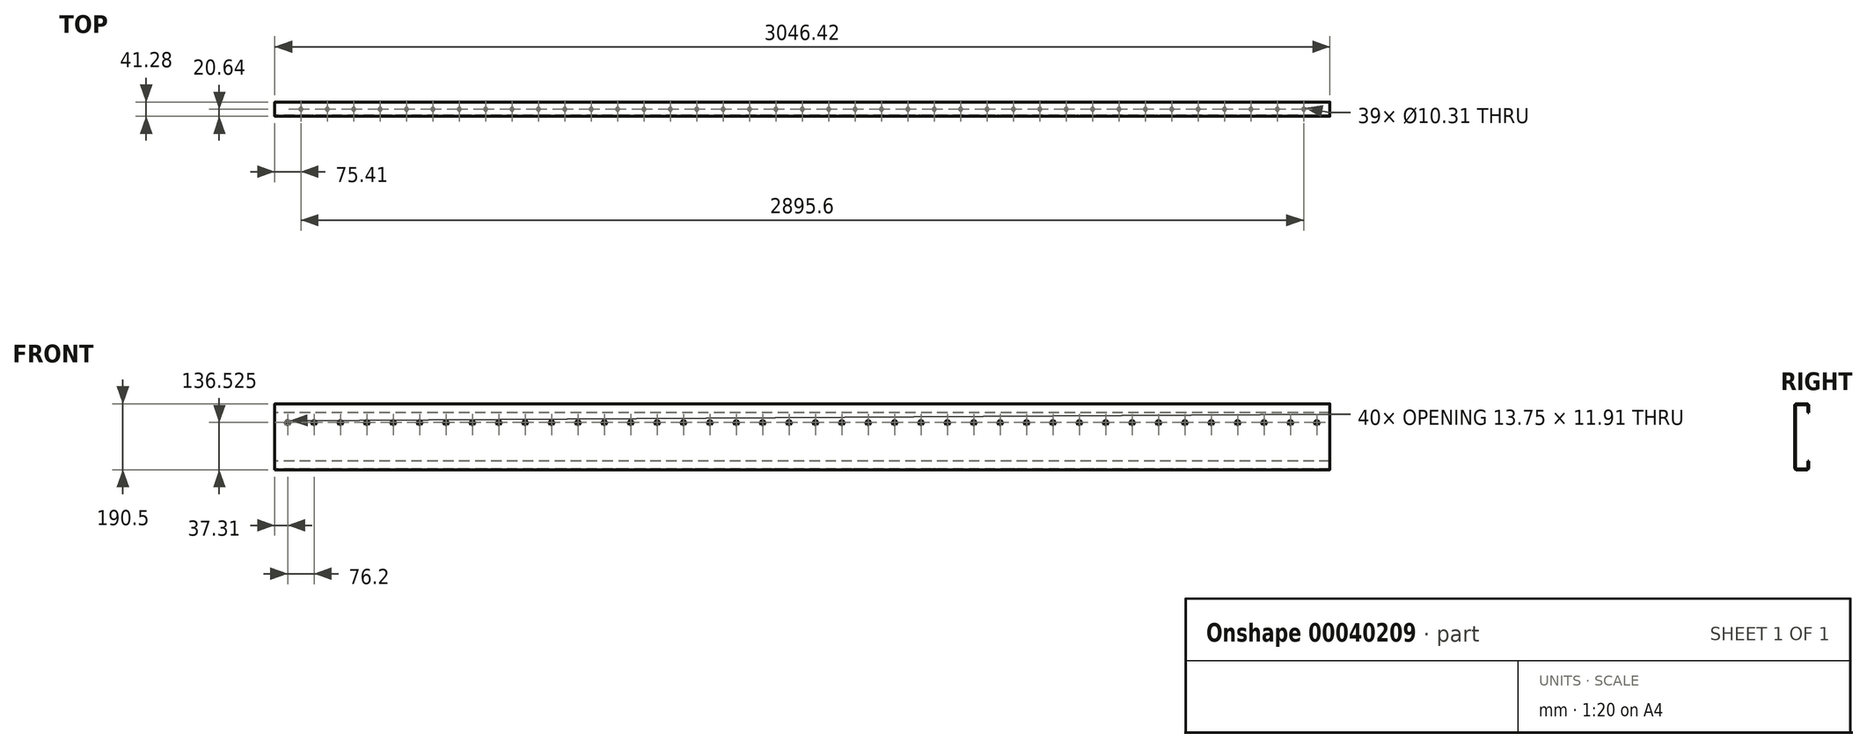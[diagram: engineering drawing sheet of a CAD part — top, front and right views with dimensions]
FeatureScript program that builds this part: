
annotation { "Feature Type Name" : "Feature", "Feature Type Description" : "" }
export const myFeature = defineFeature(function(context is Context, id is Id, definition is map)
    precondition{}
    {
        {
            var Q0;
            Q0=qCreatedBy(makeId("Right.planeOp"),FACE);
            var sketch = newSketch(context, id + "F0", { "sketchPlane" : qUnion([Q0])});
            skLineSegment(sketch, "E0", {"start": v(17.98, 69.85) * mm, "end": v(17.98, 89.42) * mm});
            skLineSegment(sketch, "E1", {"start": v(14.8, 92.6) * mm, "end": v(-14.8, 92.6) * mm});
            skLineSegment(sketch, "E2", {"start": v(-17.98, 89.42) * mm, "end": v(-17.98, -89.42) * mm});
            skLineSegment(sketch, "E3", {"start": v(-14.8, -92.6) * mm, "end": v(14.8, -92.6) * mm});
            skLineSegment(sketch, "E4", {"start": v(17.98, -89.42) * mm, "end": v(17.98, -69.85) * mm});
            skLineSegment(sketch, "E5.0", {"start": v(20.64, -88.9) * mm, "end": v(20.64, -69.85) * mm});
            skLineSegment(sketch, "E5.1", {"start": v(20.64, 69.85) * mm, "end": v(20.64, 88.9) * mm});
            skLineSegment(sketch, "E5.2", {"start": v(14.29, 95.25) * mm, "end": v(-14.29, 95.25) * mm});
            skLineSegment(sketch, "E5.3", {"start": v(-20.64, 88.9) * mm, "end": v(-20.64, -88.9) * mm});
            skLineSegment(sketch, "E5.4", {"start": v(-14.29, -95.25) * mm, "end": v(14.29, -95.25) * mm});
            skLineSegment(sketch, "E6", {"start": v(17.98, 69.85) * mm, "end": v(20.64, 69.85) * mm});
            skLineSegment(sketch, "E7", {"start": v(17.98, -69.85) * mm, "end": v(20.64, -69.85) * mm});
            skPoint(sketch, "E8.visualSharp", {"position": v(17.98, 92.6) * mm});
            skArc(sketch, "E8.filletArc", {"start": v(17.98, 89.42) * mm, "mid": v(17.05, 91.66) * mm, "end": v(14.8, 92.6) * mm});
            skPoint(sketch, "E9.visualSharp", {"position": v(17.98, -92.6) * mm});
            skArc(sketch, "E9.filletArc", {"start": v(14.8, -92.6) * mm, "mid": v(17.05, -91.66) * mm, "end": v(17.98, -89.42) * mm});
            skPoint(sketch, "E10.visualSharp", {"position": v(-17.98, -92.6) * mm});
            skArc(sketch, "E10.filletArc", {"start": v(-17.98, -89.42) * mm, "mid": v(-17.05, -91.66) * mm, "end": v(-14.8, -92.6) * mm});
            skPoint(sketch, "E11.visualSharp", {"position": v(-17.98, 92.6) * mm});
            skArc(sketch, "E11.filletArc", {"start": v(-14.8, 92.6) * mm, "mid": v(-17.05, 91.66) * mm, "end": v(-17.98, 89.42) * mm});
            skPoint(sketch, "E12.visualSharp", {"position": v(-20.64, 95.25) * mm});
            skArc(sketch, "E12.filletArc", {"start": v(-14.29, 95.25) * mm, "mid": v(-18.78, 93.4) * mm, "end": v(-20.64, 88.9) * mm});
            skPoint(sketch, "E13.visualSharp", {"position": v(20.64, 95.25) * mm});
            skArc(sketch, "E13.filletArc", {"start": v(20.64, 88.9) * mm, "mid": v(18.78, 93.4) * mm, "end": v(14.29, 95.25) * mm});
            skPoint(sketch, "E14.visualSharp", {"position": v(20.64, -95.25) * mm});
            skArc(sketch, "E14.filletArc", {"start": v(14.29, -95.25) * mm, "mid": v(18.78, -93.4) * mm, "end": v(20.64, -88.9) * mm});
            skPoint(sketch, "E15.visualSharp", {"position": v(-20.64, -95.25) * mm});
            skArc(sketch, "E15.filletArc", {"start": v(-20.64, -88.9) * mm, "mid": v(-18.78, -93.4) * mm, "end": v(-14.29, -95.25) * mm});
            skSolve(sketch);
        }
        {
            var Q0;
            Q0=makeQuery(id+"F0.imprint","IMPRINT",FACE,{"disambiguationData":[TD([[makeQuery(id+"F0.imprint","IMPRINT",EDGE,{"derivedFrom":sQuery(id+"F0.wireOp",EDGE,"E0")}),-1.0]])]});
            extrude(context, id + "F1", {"entities" : qUnion([Q0]), "endBound" : BoundingType.SYMMETRIC, "depth" : 3046.4 * mm});
        }
        {
            var Q0;
            Q0=makeQuery(id+"F1.opExtrude","SWEPT_FACE",FACE,{"disambiguationData":[OSD([sQuery(id+"F0.wireOp",EDGE,"E5.4")])]});
            var sketch = newSketch(context, id + "F2", { "sketchPlane" : qUnion([Q0])});
            skPoint(sketch, "E16", {"position": v(-1447.8, 0) * mm});
            skPoint(sketch, "E16.positionSnap0", {"position": v(-1523.2, 0) * mm});
            skPoint(sketch, "E17", {"position": v(-1371.6, 0) * mm});
            skPoint(sketch, "E18.1.0.0", {"position": v(-1295.4, 0) * mm});
            skPoint(sketch, "E18.2.0.0", {"position": v(-1219.2, 0) * mm});
            skPoint(sketch, "E18.3.0.0", {"position": v(-1143, 0) * mm});
            skPoint(sketch, "E18.4.0.0", {"position": v(-1066.8, 0) * mm});
            skPoint(sketch, "E18.5.0.0", {"position": v(-990.6, 0) * mm});
            skPoint(sketch, "E18.6.0.0", {"position": v(-914.4, 0) * mm});
            skPoint(sketch, "E18.7.0.0", {"position": v(-838.2, 0) * mm});
            skPoint(sketch, "E18.8.0.0", {"position": v(-762, 0) * mm});
            skPoint(sketch, "E18.9.0.0", {"position": v(-685.8, 0) * mm});
            skPoint(sketch, "E18.10.0.0", {"position": v(-609.6, 0) * mm});
            skPoint(sketch, "E18.11.0.0", {"position": v(-533.4, 0) * mm});
            skPoint(sketch, "E18.12.0.0", {"position": v(-457.2, 0) * mm});
            skPoint(sketch, "E18.13.0.0", {"position": v(-381, 0) * mm});
            skPoint(sketch, "E18.14.0.0", {"position": v(-304.8, 0) * mm});
            skPoint(sketch, "E18.15.0.0", {"position": v(-228.6, 0) * mm});
            skPoint(sketch, "E18.16.0.0", {"position": v(-152.4, 0) * mm});
            skPoint(sketch, "E18.17.0.0", {"position": v(-76.2, 0) * mm});
            skPoint(sketch, "E18.18.0.0", {"position": v(0, 0) * mm});
            skPoint(sketch, "E18.19.0.0", {"position": v(76.2, 0) * mm});
            skPoint(sketch, "E18.20.0.0", {"position": v(152.4, 0) * mm});
            skPoint(sketch, "E18.21.0.0", {"position": v(228.6, 0) * mm});
            skPoint(sketch, "E18.22.0.0", {"position": v(304.8, 0) * mm});
            skPoint(sketch, "E18.23.0.0", {"position": v(381, 0) * mm});
            skPoint(sketch, "E18.24.0.0", {"position": v(457.2, 0) * mm});
            skPoint(sketch, "E18.25.0.0", {"position": v(533.4, 0) * mm});
            skPoint(sketch, "E18.26.0.0", {"position": v(609.6, 0) * mm});
            skPoint(sketch, "E18.27.0.0", {"position": v(685.8, 0) * mm});
            skPoint(sketch, "E18.28.0.0", {"position": v(762, 0) * mm});
            skPoint(sketch, "E18.29.0.0", {"position": v(838.2, 0) * mm});
            skPoint(sketch, "E18.30.0.0", {"position": v(914.4, 0) * mm});
            skPoint(sketch, "E18.31.0.0", {"position": v(990.6, 0) * mm});
            skPoint(sketch, "E18.32.0.0", {"position": v(1066.8, 0) * mm});
            skPoint(sketch, "E18.33.0.0", {"position": v(1143, 0) * mm});
            skPoint(sketch, "E18.34.0.0", {"position": v(1219.2, 0) * mm});
            skLineSegment(sketch, "E18.direction1", {"start": v(-1371.6, 0) * mm, "end": v(-1295.4, 0) * mm, "construction": true});
            skPoint(sketch, "E19.0.35.0", {"position": v(1295.4, 0) * mm});
            skPoint(sketch, "E19.0.36.0", {"position": v(1371.6, 0) * mm});
            skPoint(sketch, "E20.0.37.0", {"position": v(1447.8, 0) * mm});
            skSolve(sketch);
        }
        {
            var Q0;
            Q0=sQuery(id+"F2.wireOp",VERTEX,"E16");
            var Q1;
            Q1=sQuery(id+"F2.wireOp",VERTEX,"E17");
            var Q2;
            Q2=sQuery(id+"F2.wireOp",VERTEX,"E18.1.0.0");
            var Q3;
            Q3=sQuery(id+"F2.wireOp",VERTEX,"E18.6.0.0");
            var Q4;
            Q4=sQuery(id+"F2.wireOp",VERTEX,"E18.7.0.0");
            var Q5;
            Q5=sQuery(id+"F2.wireOp",VERTEX,"E18.8.0.0");
            var Q6;
            Q6=sQuery(id+"F2.wireOp",VERTEX,"E18.9.0.0");
            var Q7;
            Q7=sQuery(id+"F2.wireOp",VERTEX,"E18.10.0.0");
            var Q8;
            Q8=sQuery(id+"F2.wireOp",VERTEX,"E18.11.0.0");
            var Q9;
            Q9=sQuery(id+"F2.wireOp",VERTEX,"E18.2.0.0");
            var Q10;
            Q10=sQuery(id+"F2.wireOp",VERTEX,"E18.5.0.0");
            var Q11;
            Q11=sQuery(id+"F2.wireOp",VERTEX,"E18.4.0.0");
            var Q12;
            Q12=sQuery(id+"F2.wireOp",VERTEX,"E18.3.0.0");
            var Q13;
            Q13=sQuery(id+"F2.wireOp",VERTEX,"E18.24.0.0");
            var Q14;
            Q14=sQuery(id+"F2.wireOp",VERTEX,"E18.23.0.0");
            var Q15;
            Q15=sQuery(id+"F2.wireOp",VERTEX,"E18.28.0.0");
            var Q16;
            Q16=sQuery(id+"F2.wireOp",VERTEX,"E18.22.0.0");
            var Q17;
            Q17=sQuery(id+"F2.wireOp",VERTEX,"E20.0.37.0");
            var Q18;
            Q18=sQuery(id+"F2.wireOp",VERTEX,"E18.21.0.0");
            var Q19;
            Q19=sQuery(id+"F2.wireOp",VERTEX,"E19.0.36.0");
            var Q20;
            Q20=sQuery(id+"F2.wireOp",VERTEX,"E18.20.0.0");
            var Q21;
            Q21=sQuery(id+"F2.wireOp",VERTEX,"E19.0.35.0");
            var Q22;
            Q22=sQuery(id+"F2.wireOp",VERTEX,"E18.19.0.0");
            var Q23;
            Q23=sQuery(id+"F2.wireOp",VERTEX,"E18.18.0.0");
            var Q24;
            Q24=sQuery(id+"F2.wireOp",VERTEX,"E18.17.0.0");
            var Q25;
            Q25=sQuery(id+"F2.wireOp",VERTEX,"E18.34.0.0");
            var Q26;
            Q26=sQuery(id+"F2.wireOp",VERTEX,"E18.27.0.0");
            var Q27;
            Q27=sQuery(id+"F2.wireOp",VERTEX,"E18.16.0.0");
            var Q28;
            Q28=sQuery(id+"F2.wireOp",VERTEX,"E18.33.0.0");
            var Q29;
            Q29=sQuery(id+"F2.wireOp",VERTEX,"E18.26.0.0");
            var Q30;
            Q30=sQuery(id+"F2.wireOp",VERTEX,"E18.15.0.0");
            var Q31;
            Q31=sQuery(id+"F2.wireOp",VERTEX,"E18.25.0.0");
            var Q32;
            Q32=sQuery(id+"F2.wireOp",VERTEX,"E18.32.0.0");
            var Q33;
            Q33=sQuery(id+"F2.wireOp",VERTEX,"E18.14.0.0");
            var Q34;
            Q34=sQuery(id+"F2.wireOp",VERTEX,"E18.31.0.0");
            var Q35;
            Q35=sQuery(id+"F2.wireOp",VERTEX,"E18.13.0.0");
            var Q36;
            Q36=sQuery(id+"F2.wireOp",VERTEX,"E18.30.0.0");
            var Q37;
            Q37=sQuery(id+"F2.wireOp",VERTEX,"E18.12.0.0");
            var Q38;
            Q38=sQuery(id+"F2.wireOp",VERTEX,"E18.29.0.0");
            var Q39;
            Q39=makeQuery(id+"F1.opExtrude","SWEPT_BODY",BODY,{"disambiguationData":[OSD([sQuery(id+"F0.wireOp",EDGE,"E0"),sQuery(id+"F0.wireOp",EDGE,"E1"),sQuery(id+"F0.wireOp",EDGE,"E2"),sQuery(id+"F0.wireOp",EDGE,"E3"),sQuery(id+"F0.wireOp",EDGE,"E4"),sQuery(id+"F0.wireOp",EDGE,"E5.0"),sQuery(id+"F0.wireOp",EDGE,"E5.1"),sQuery(id+"F0.wireOp",EDGE,"E5.2"),sQuery(id+"F0.wireOp",EDGE,"E5.3"),sQuery(id+"F0.wireOp",EDGE,"E5.4"),sQuery(id+"F0.wireOp",EDGE,"E6"),sQuery(id+"F0.wireOp",EDGE,"E7"),sQuery(id+"F0.wireOp",EDGE,"E8.filletArc"),sQuery(id+"F0.wireOp",EDGE,"E9.filletArc"),sQuery(id+"F0.wireOp",EDGE,"E10.filletArc"),sQuery(id+"F0.wireOp",EDGE,"E11.filletArc"),sQuery(id+"F0.wireOp",EDGE,"E12.filletArc"),sQuery(id+"F0.wireOp",EDGE,"E13.filletArc"),sQuery(id+"F0.wireOp",EDGE,"E14.filletArc"),sQuery(id+"F0.wireOp",EDGE,"E15.filletArc")])]});
            hole(context, id + "F3", {"style" : HoleStyle.SIMPLE, "holeDiameter" : 10.3 * mm, "endStyle" : HoleEndStyle.BLIND, "holeDepth" : 38.1 * mm, "locations" : qUnion([Q0, Q1, Q2, Q3, Q4, Q5, Q6, Q7, Q8, Q9, Q10, Q11, Q12, Q13, Q14, Q15, Q16, Q17, Q18, Q19, Q20, Q21, Q22, Q23, Q24, Q25, Q26, Q27, Q28, Q29, Q30, Q31, Q32, Q33, Q34, Q35, Q36, Q37, Q38]), "scope" : qUnion([Q39])});
        }
        {
            var Q0;
            Q0=makeQuery(id+"F1.opExtrude","SWEPT_FACE",FACE,{"disambiguationData":[OSD([sQuery(id+"F0.wireOp",EDGE,"E5.3")])]});
            var sketch = newSketch(context, id + "F4", { "sketchPlane" : qUnion([Q0])});
            skLineSegment(sketch, "E21", {"start": v(-1523.2, 41.28) * mm, "end": v(-1485.9, 41.28) * mm, "construction": true});
            skLineSegment(sketch, "E22.0", {"start": v(1523.2, 95.25) * mm, "end": v(-1523.2, 95.25) * mm, "construction": true});
            skCircle(sketch, "E23.cCircle", {"center": v(-1485.9, 41.28) * mm, "radius": 6.87 * mm, "construction": true});
            skLineSegment(sketch, "E23.0", {"start": v(-1492.77, 41.27) * mm, "end": v(-1489.34, 47.23) * mm});
            skLineSegment(sketch, "E23.1", {"start": v(-1489.34, 47.23) * mm, "end": v(-1482.46, 47.23) * mm});
            skLineSegment(sketch, "E23.2", {"start": v(-1482.46, 47.23) * mm, "end": v(-1479.03, 41.27) * mm});
            skLineSegment(sketch, "E23.3", {"start": v(-1479.03, 41.27) * mm, "end": v(-1482.46, 35.32) * mm});
            skLineSegment(sketch, "E23.4", {"start": v(-1482.46, 35.32) * mm, "end": v(-1489.34, 35.32) * mm});
            skLineSegment(sketch, "E23.5", {"start": v(-1489.34, 35.32) * mm, "end": v(-1492.77, 41.27) * mm});
            skLineSegment(sketch, "E24.1.0.0", {"start": v(-1406.26, 35.32) * mm, "end": v(-1413.14, 35.32) * mm});
            skLineSegment(sketch, "E24.1.0.1", {"start": v(-1402.83, 41.28) * mm, "end": v(-1406.26, 35.32) * mm});
            skLineSegment(sketch, "E24.1.0.2", {"start": v(-1413.14, 47.23) * mm, "end": v(-1406.26, 47.23) * mm});
            skLineSegment(sketch, "E24.1.0.3", {"start": v(-1406.26, 47.23) * mm, "end": v(-1402.83, 41.27) * mm});
            skCircle(sketch, "E24.1.0.4", {"center": v(-1409.7, 41.28) * mm, "radius": 6.87 * mm, "construction": true});
            skLineSegment(sketch, "E24.1.0.5", {"start": v(-1413.14, 35.32) * mm, "end": v(-1416.57, 41.27) * mm});
            skLineSegment(sketch, "E24.1.0.6", {"start": v(-1416.57, 41.28) * mm, "end": v(-1413.14, 47.23) * mm});
            skLineSegment(sketch, "E24.2.0.0", {"start": v(-1330.06, 35.32) * mm, "end": v(-1336.94, 35.32) * mm});
            skLineSegment(sketch, "E24.2.0.1", {"start": v(-1326.63, 41.28) * mm, "end": v(-1330.06, 35.32) * mm});
            skLineSegment(sketch, "E24.2.0.2", {"start": v(-1336.94, 47.23) * mm, "end": v(-1330.06, 47.23) * mm});
            skLineSegment(sketch, "E24.2.0.3", {"start": v(-1330.06, 47.23) * mm, "end": v(-1326.63, 41.27) * mm});
            skCircle(sketch, "E24.2.0.4", {"center": v(-1333.5, 41.28) * mm, "radius": 6.87 * mm, "construction": true});
            skLineSegment(sketch, "E24.2.0.5", {"start": v(-1336.94, 35.32) * mm, "end": v(-1340.37, 41.27) * mm});
            skLineSegment(sketch, "E24.2.0.6", {"start": v(-1340.37, 41.28) * mm, "end": v(-1336.94, 47.23) * mm});
            skLineSegment(sketch, "E24.3.0.0", {"start": v(-1253.86, 35.32) * mm, "end": v(-1260.74, 35.32) * mm});
            skLineSegment(sketch, "E24.3.0.1", {"start": v(-1250.43, 41.28) * mm, "end": v(-1253.86, 35.32) * mm});
            skLineSegment(sketch, "E24.3.0.2", {"start": v(-1260.74, 47.23) * mm, "end": v(-1253.86, 47.23) * mm});
            skLineSegment(sketch, "E24.3.0.3", {"start": v(-1253.86, 47.23) * mm, "end": v(-1250.43, 41.27) * mm});
            skCircle(sketch, "E24.3.0.4", {"center": v(-1257.3, 41.28) * mm, "radius": 6.87 * mm, "construction": true});
            skLineSegment(sketch, "E24.3.0.5", {"start": v(-1260.74, 35.32) * mm, "end": v(-1264.17, 41.27) * mm});
            skLineSegment(sketch, "E24.3.0.6", {"start": v(-1264.17, 41.28) * mm, "end": v(-1260.74, 47.23) * mm});
            skLineSegment(sketch, "E24.4.0.0", {"start": v(-1177.66, 35.32) * mm, "end": v(-1184.54, 35.32) * mm});
            skLineSegment(sketch, "E24.4.0.1", {"start": v(-1174.23, 41.28) * mm, "end": v(-1177.66, 35.32) * mm});
            skLineSegment(sketch, "E24.4.0.2", {"start": v(-1184.54, 47.23) * mm, "end": v(-1177.66, 47.23) * mm});
            skLineSegment(sketch, "E24.4.0.3", {"start": v(-1177.66, 47.23) * mm, "end": v(-1174.23, 41.27) * mm});
            skCircle(sketch, "E24.4.0.4", {"center": v(-1181.1, 41.28) * mm, "radius": 6.87 * mm, "construction": true});
            skLineSegment(sketch, "E24.4.0.5", {"start": v(-1184.54, 35.32) * mm, "end": v(-1187.97, 41.27) * mm});
            skLineSegment(sketch, "E24.4.0.6", {"start": v(-1187.97, 41.28) * mm, "end": v(-1184.54, 47.23) * mm});
            skLineSegment(sketch, "E24.5.0.0", {"start": v(-1101.46, 35.32) * mm, "end": v(-1108.34, 35.32) * mm});
            skLineSegment(sketch, "E24.5.0.1", {"start": v(-1098.03, 41.28) * mm, "end": v(-1101.46, 35.32) * mm});
            skLineSegment(sketch, "E24.5.0.2", {"start": v(-1108.34, 47.23) * mm, "end": v(-1101.46, 47.23) * mm});
            skLineSegment(sketch, "E24.5.0.3", {"start": v(-1101.46, 47.23) * mm, "end": v(-1098.03, 41.27) * mm});
            skCircle(sketch, "E24.5.0.4", {"center": v(-1104.9, 41.28) * mm, "radius": 6.87 * mm, "construction": true});
            skLineSegment(sketch, "E24.5.0.5", {"start": v(-1108.34, 35.32) * mm, "end": v(-1111.77, 41.27) * mm});
            skLineSegment(sketch, "E24.5.0.6", {"start": v(-1111.77, 41.28) * mm, "end": v(-1108.34, 47.23) * mm});
            skLineSegment(sketch, "E24.6.0.0", {"start": v(-1025.26, 35.32) * mm, "end": v(-1032.14, 35.32) * mm});
            skLineSegment(sketch, "E24.6.0.1", {"start": v(-1021.83, 41.28) * mm, "end": v(-1025.26, 35.32) * mm});
            skLineSegment(sketch, "E24.6.0.2", {"start": v(-1032.14, 47.23) * mm, "end": v(-1025.26, 47.23) * mm});
            skLineSegment(sketch, "E24.6.0.3", {"start": v(-1025.26, 47.23) * mm, "end": v(-1021.83, 41.27) * mm});
            skCircle(sketch, "E24.6.0.4", {"center": v(-1028.7, 41.28) * mm, "radius": 6.87 * mm, "construction": true});
            skLineSegment(sketch, "E24.6.0.5", {"start": v(-1032.14, 35.32) * mm, "end": v(-1035.57, 41.27) * mm});
            skLineSegment(sketch, "E24.6.0.6", {"start": v(-1035.57, 41.28) * mm, "end": v(-1032.14, 47.23) * mm});
            skLineSegment(sketch, "E24.7.0.0", {"start": v(-949.06, 35.32) * mm, "end": v(-955.94, 35.32) * mm});
            skLineSegment(sketch, "E24.7.0.1", {"start": v(-945.63, 41.28) * mm, "end": v(-949.06, 35.32) * mm});
            skLineSegment(sketch, "E24.7.0.2", {"start": v(-955.94, 47.23) * mm, "end": v(-949.06, 47.23) * mm});
            skLineSegment(sketch, "E24.7.0.3", {"start": v(-949.06, 47.23) * mm, "end": v(-945.63, 41.27) * mm});
            skCircle(sketch, "E24.7.0.4", {"center": v(-952.5, 41.28) * mm, "radius": 6.87 * mm, "construction": true});
            skLineSegment(sketch, "E24.7.0.5", {"start": v(-955.94, 35.32) * mm, "end": v(-959.37, 41.27) * mm});
            skLineSegment(sketch, "E24.7.0.6", {"start": v(-959.37, 41.28) * mm, "end": v(-955.94, 47.23) * mm});
            skLineSegment(sketch, "E24.8.0.0", {"start": v(-872.86, 35.32) * mm, "end": v(-879.74, 35.32) * mm});
            skLineSegment(sketch, "E24.8.0.1", {"start": v(-869.43, 41.28) * mm, "end": v(-872.86, 35.32) * mm});
            skLineSegment(sketch, "E24.8.0.2", {"start": v(-879.74, 47.23) * mm, "end": v(-872.86, 47.23) * mm});
            skLineSegment(sketch, "E24.8.0.3", {"start": v(-872.86, 47.23) * mm, "end": v(-869.43, 41.27) * mm});
            skCircle(sketch, "E24.8.0.4", {"center": v(-876.3, 41.28) * mm, "radius": 6.87 * mm, "construction": true});
            skLineSegment(sketch, "E24.8.0.5", {"start": v(-879.74, 35.32) * mm, "end": v(-883.17, 41.27) * mm});
            skLineSegment(sketch, "E24.8.0.6", {"start": v(-883.17, 41.28) * mm, "end": v(-879.74, 47.23) * mm});
            skLineSegment(sketch, "E24.9.0.0", {"start": v(-796.66, 35.32) * mm, "end": v(-803.54, 35.32) * mm});
            skLineSegment(sketch, "E24.9.0.1", {"start": v(-793.23, 41.28) * mm, "end": v(-796.66, 35.32) * mm});
            skLineSegment(sketch, "E24.9.0.2", {"start": v(-803.54, 47.23) * mm, "end": v(-796.66, 47.23) * mm});
            skLineSegment(sketch, "E24.9.0.3", {"start": v(-796.66, 47.23) * mm, "end": v(-793.23, 41.27) * mm});
            skCircle(sketch, "E24.9.0.4", {"center": v(-800.1, 41.28) * mm, "radius": 6.87 * mm, "construction": true});
            skLineSegment(sketch, "E24.9.0.5", {"start": v(-803.54, 35.32) * mm, "end": v(-806.97, 41.27) * mm});
            skLineSegment(sketch, "E24.9.0.6", {"start": v(-806.97, 41.28) * mm, "end": v(-803.54, 47.23) * mm});
            skLineSegment(sketch, "E24.10.0.0", {"start": v(-720.46, 35.32) * mm, "end": v(-727.34, 35.32) * mm});
            skLineSegment(sketch, "E24.10.0.1", {"start": v(-717.03, 41.28) * mm, "end": v(-720.46, 35.32) * mm});
            skLineSegment(sketch, "E24.10.0.2", {"start": v(-727.34, 47.23) * mm, "end": v(-720.46, 47.23) * mm});
            skLineSegment(sketch, "E24.10.0.3", {"start": v(-720.46, 47.23) * mm, "end": v(-717.03, 41.27) * mm});
            skCircle(sketch, "E24.10.0.4", {"center": v(-723.9, 41.28) * mm, "radius": 6.87 * mm, "construction": true});
            skLineSegment(sketch, "E24.10.0.5", {"start": v(-727.34, 35.32) * mm, "end": v(-730.77, 41.27) * mm});
            skLineSegment(sketch, "E24.10.0.6", {"start": v(-730.77, 41.28) * mm, "end": v(-727.34, 47.23) * mm});
            skLineSegment(sketch, "E24.11.0.0", {"start": v(-644.26, 35.32) * mm, "end": v(-651.14, 35.32) * mm});
            skLineSegment(sketch, "E24.11.0.1", {"start": v(-640.83, 41.28) * mm, "end": v(-644.26, 35.32) * mm});
            skLineSegment(sketch, "E24.11.0.2", {"start": v(-651.14, 47.23) * mm, "end": v(-644.26, 47.23) * mm});
            skLineSegment(sketch, "E24.11.0.3", {"start": v(-644.26, 47.23) * mm, "end": v(-640.83, 41.27) * mm});
            skCircle(sketch, "E24.11.0.4", {"center": v(-647.7, 41.28) * mm, "radius": 6.87 * mm, "construction": true});
            skLineSegment(sketch, "E24.11.0.5", {"start": v(-651.14, 35.32) * mm, "end": v(-654.57, 41.27) * mm});
            skLineSegment(sketch, "E24.11.0.6", {"start": v(-654.57, 41.28) * mm, "end": v(-651.14, 47.23) * mm});
            skLineSegment(sketch, "E24.12.0.0", {"start": v(-568.06, 35.32) * mm, "end": v(-574.94, 35.32) * mm});
            skLineSegment(sketch, "E24.12.0.1", {"start": v(-564.63, 41.28) * mm, "end": v(-568.06, 35.32) * mm});
            skLineSegment(sketch, "E24.12.0.2", {"start": v(-574.94, 47.23) * mm, "end": v(-568.06, 47.23) * mm});
            skLineSegment(sketch, "E24.12.0.3", {"start": v(-568.06, 47.23) * mm, "end": v(-564.63, 41.27) * mm});
            skCircle(sketch, "E24.12.0.4", {"center": v(-571.5, 41.28) * mm, "radius": 6.87 * mm, "construction": true});
            skLineSegment(sketch, "E24.12.0.5", {"start": v(-574.94, 35.32) * mm, "end": v(-578.37, 41.27) * mm});
            skLineSegment(sketch, "E24.12.0.6", {"start": v(-578.37, 41.28) * mm, "end": v(-574.94, 47.23) * mm});
            skLineSegment(sketch, "E24.13.0.0", {"start": v(-491.86, 35.32) * mm, "end": v(-498.74, 35.32) * mm});
            skLineSegment(sketch, "E24.13.0.1", {"start": v(-488.43, 41.28) * mm, "end": v(-491.86, 35.32) * mm});
            skLineSegment(sketch, "E24.13.0.2", {"start": v(-498.74, 47.23) * mm, "end": v(-491.86, 47.23) * mm});
            skLineSegment(sketch, "E24.13.0.3", {"start": v(-491.86, 47.23) * mm, "end": v(-488.43, 41.27) * mm});
            skCircle(sketch, "E24.13.0.4", {"center": v(-495.3, 41.28) * mm, "radius": 6.87 * mm, "construction": true});
            skLineSegment(sketch, "E24.13.0.5", {"start": v(-498.74, 35.32) * mm, "end": v(-502.17, 41.27) * mm});
            skLineSegment(sketch, "E24.13.0.6", {"start": v(-502.17, 41.28) * mm, "end": v(-498.74, 47.23) * mm});
            skLineSegment(sketch, "E24.14.0.0", {"start": v(-415.66, 35.32) * mm, "end": v(-422.54, 35.32) * mm});
            skLineSegment(sketch, "E24.14.0.1", {"start": v(-412.23, 41.28) * mm, "end": v(-415.66, 35.32) * mm});
            skLineSegment(sketch, "E24.14.0.2", {"start": v(-422.54, 47.23) * mm, "end": v(-415.66, 47.23) * mm});
            skLineSegment(sketch, "E24.14.0.3", {"start": v(-415.66, 47.23) * mm, "end": v(-412.23, 41.28) * mm});
            skCircle(sketch, "E24.14.0.4", {"center": v(-419.1, 41.28) * mm, "radius": 6.87 * mm, "construction": true});
            skLineSegment(sketch, "E24.14.0.5", {"start": v(-422.54, 35.32) * mm, "end": v(-425.97, 41.27) * mm});
            skLineSegment(sketch, "E24.14.0.6", {"start": v(-425.97, 41.27) * mm, "end": v(-422.54, 47.23) * mm});
            skLineSegment(sketch, "E24.15.0.0", {"start": v(-339.46, 35.32) * mm, "end": v(-346.34, 35.32) * mm});
            skLineSegment(sketch, "E24.15.0.1", {"start": v(-336.03, 41.28) * mm, "end": v(-339.46, 35.32) * mm});
            skLineSegment(sketch, "E24.15.0.2", {"start": v(-346.34, 47.23) * mm, "end": v(-339.46, 47.23) * mm});
            skLineSegment(sketch, "E24.15.0.3", {"start": v(-339.46, 47.23) * mm, "end": v(-336.03, 41.28) * mm});
            skCircle(sketch, "E24.15.0.4", {"center": v(-342.9, 41.28) * mm, "radius": 6.87 * mm, "construction": true});
            skLineSegment(sketch, "E24.15.0.5", {"start": v(-346.34, 35.32) * mm, "end": v(-349.77, 41.27) * mm});
            skLineSegment(sketch, "E24.15.0.6", {"start": v(-349.77, 41.27) * mm, "end": v(-346.34, 47.23) * mm});
            skLineSegment(sketch, "E24.16.0.0", {"start": v(-263.26, 35.32) * mm, "end": v(-270.14, 35.32) * mm});
            skLineSegment(sketch, "E24.16.0.1", {"start": v(-259.83, 41.28) * mm, "end": v(-263.26, 35.32) * mm});
            skLineSegment(sketch, "E24.16.0.2", {"start": v(-270.14, 47.23) * mm, "end": v(-263.26, 47.23) * mm});
            skLineSegment(sketch, "E24.16.0.3", {"start": v(-263.26, 47.23) * mm, "end": v(-259.83, 41.28) * mm});
            skCircle(sketch, "E24.16.0.4", {"center": v(-266.7, 41.28) * mm, "radius": 6.87 * mm, "construction": true});
            skLineSegment(sketch, "E24.16.0.5", {"start": v(-270.14, 35.32) * mm, "end": v(-273.57, 41.27) * mm});
            skLineSegment(sketch, "E24.16.0.6", {"start": v(-273.57, 41.27) * mm, "end": v(-270.14, 47.23) * mm});
            skLineSegment(sketch, "E24.17.0.0", {"start": v(-187.06, 35.32) * mm, "end": v(-193.94, 35.32) * mm});
            skLineSegment(sketch, "E24.17.0.1", {"start": v(-183.63, 41.28) * mm, "end": v(-187.06, 35.32) * mm});
            skLineSegment(sketch, "E24.17.0.2", {"start": v(-193.94, 47.23) * mm, "end": v(-187.06, 47.23) * mm});
            skLineSegment(sketch, "E24.17.0.3", {"start": v(-187.06, 47.23) * mm, "end": v(-183.63, 41.28) * mm});
            skCircle(sketch, "E24.17.0.4", {"center": v(-190.5, 41.28) * mm, "radius": 6.87 * mm, "construction": true});
            skLineSegment(sketch, "E24.17.0.5", {"start": v(-193.94, 35.32) * mm, "end": v(-197.37, 41.27) * mm});
            skLineSegment(sketch, "E24.17.0.6", {"start": v(-197.37, 41.27) * mm, "end": v(-193.94, 47.23) * mm});
            skLineSegment(sketch, "E24.18.0.0", {"start": v(-110.86, 35.32) * mm, "end": v(-117.74, 35.32) * mm});
            skLineSegment(sketch, "E24.18.0.1", {"start": v(-107.43, 41.28) * mm, "end": v(-110.86, 35.32) * mm});
            skLineSegment(sketch, "E24.18.0.2", {"start": v(-117.74, 47.23) * mm, "end": v(-110.86, 47.23) * mm});
            skLineSegment(sketch, "E24.18.0.3", {"start": v(-110.86, 47.23) * mm, "end": v(-107.43, 41.28) * mm});
            skCircle(sketch, "E24.18.0.4", {"center": v(-114.3, 41.28) * mm, "radius": 6.87 * mm, "construction": true});
            skLineSegment(sketch, "E24.18.0.5", {"start": v(-117.74, 35.32) * mm, "end": v(-121.17, 41.27) * mm});
            skLineSegment(sketch, "E24.18.0.6", {"start": v(-121.17, 41.27) * mm, "end": v(-117.74, 47.23) * mm});
            skLineSegment(sketch, "E24.19.0.0", {"start": v(-34.66, 35.32) * mm, "end": v(-41.54, 35.32) * mm});
            skLineSegment(sketch, "E24.19.0.1", {"start": v(-31.23, 41.28) * mm, "end": v(-34.66, 35.32) * mm});
            skLineSegment(sketch, "E24.19.0.2", {"start": v(-41.54, 47.23) * mm, "end": v(-34.66, 47.23) * mm});
            skLineSegment(sketch, "E24.19.0.3", {"start": v(-34.66, 47.23) * mm, "end": v(-31.23, 41.28) * mm});
            skCircle(sketch, "E24.19.0.4", {"center": v(-38.1, 41.28) * mm, "radius": 6.87 * mm, "construction": true});
            skLineSegment(sketch, "E24.19.0.5", {"start": v(-41.54, 35.32) * mm, "end": v(-44.97, 41.27) * mm});
            skLineSegment(sketch, "E24.19.0.6", {"start": v(-44.97, 41.27) * mm, "end": v(-41.54, 47.23) * mm});
            skLineSegment(sketch, "E24.20.0.0", {"start": v(41.54, 35.32) * mm, "end": v(34.66, 35.32) * mm});
            skLineSegment(sketch, "E24.20.0.1", {"start": v(44.97, 41.28) * mm, "end": v(41.54, 35.32) * mm});
            skLineSegment(sketch, "E24.20.0.2", {"start": v(34.66, 47.23) * mm, "end": v(41.54, 47.23) * mm});
            skLineSegment(sketch, "E24.20.0.3", {"start": v(41.54, 47.23) * mm, "end": v(44.97, 41.28) * mm});
            skCircle(sketch, "E24.20.0.4", {"center": v(38.1, 41.28) * mm, "radius": 6.87 * mm, "construction": true});
            skLineSegment(sketch, "E24.20.0.5", {"start": v(34.66, 35.32) * mm, "end": v(31.23, 41.27) * mm});
            skLineSegment(sketch, "E24.20.0.6", {"start": v(31.23, 41.27) * mm, "end": v(34.66, 47.23) * mm});
            skLineSegment(sketch, "E24.21.0.0", {"start": v(117.74, 35.32) * mm, "end": v(110.86, 35.32) * mm});
            skLineSegment(sketch, "E24.21.0.1", {"start": v(121.17, 41.28) * mm, "end": v(117.74, 35.32) * mm});
            skLineSegment(sketch, "E24.21.0.2", {"start": v(110.86, 47.23) * mm, "end": v(117.74, 47.23) * mm});
            skLineSegment(sketch, "E24.21.0.3", {"start": v(117.74, 47.23) * mm, "end": v(121.17, 41.28) * mm});
            skCircle(sketch, "E24.21.0.4", {"center": v(114.3, 41.28) * mm, "radius": 6.87 * mm, "construction": true});
            skLineSegment(sketch, "E24.21.0.5", {"start": v(110.86, 35.32) * mm, "end": v(107.43, 41.27) * mm});
            skLineSegment(sketch, "E24.21.0.6", {"start": v(107.43, 41.27) * mm, "end": v(110.86, 47.23) * mm});
            skLineSegment(sketch, "E24.22.0.0", {"start": v(193.94, 35.32) * mm, "end": v(187.06, 35.32) * mm});
            skLineSegment(sketch, "E24.22.0.1", {"start": v(197.37, 41.28) * mm, "end": v(193.94, 35.32) * mm});
            skLineSegment(sketch, "E24.22.0.2", {"start": v(187.06, 47.23) * mm, "end": v(193.94, 47.23) * mm});
            skLineSegment(sketch, "E24.22.0.3", {"start": v(193.94, 47.23) * mm, "end": v(197.37, 41.28) * mm});
            skCircle(sketch, "E24.22.0.4", {"center": v(190.5, 41.28) * mm, "radius": 6.87 * mm, "construction": true});
            skLineSegment(sketch, "E24.22.0.5", {"start": v(187.06, 35.32) * mm, "end": v(183.63, 41.27) * mm});
            skLineSegment(sketch, "E24.22.0.6", {"start": v(183.63, 41.27) * mm, "end": v(187.06, 47.23) * mm});
            skLineSegment(sketch, "E24.23.0.0", {"start": v(270.14, 35.32) * mm, "end": v(263.26, 35.32) * mm});
            skLineSegment(sketch, "E24.23.0.1", {"start": v(273.57, 41.28) * mm, "end": v(270.14, 35.32) * mm});
            skLineSegment(sketch, "E24.23.0.2", {"start": v(263.26, 47.23) * mm, "end": v(270.14, 47.23) * mm});
            skLineSegment(sketch, "E24.23.0.3", {"start": v(270.14, 47.23) * mm, "end": v(273.57, 41.28) * mm});
            skCircle(sketch, "E24.23.0.4", {"center": v(266.7, 41.28) * mm, "radius": 6.87 * mm, "construction": true});
            skLineSegment(sketch, "E24.23.0.5", {"start": v(263.26, 35.32) * mm, "end": v(259.83, 41.27) * mm});
            skLineSegment(sketch, "E24.23.0.6", {"start": v(259.83, 41.27) * mm, "end": v(263.26, 47.23) * mm});
            skLineSegment(sketch, "E24.24.0.0", {"start": v(346.34, 35.32) * mm, "end": v(339.46, 35.32) * mm});
            skLineSegment(sketch, "E24.24.0.1", {"start": v(349.77, 41.28) * mm, "end": v(346.34, 35.32) * mm});
            skLineSegment(sketch, "E24.24.0.2", {"start": v(339.46, 47.23) * mm, "end": v(346.34, 47.23) * mm});
            skLineSegment(sketch, "E24.24.0.3", {"start": v(346.34, 47.23) * mm, "end": v(349.77, 41.28) * mm});
            skCircle(sketch, "E24.24.0.4", {"center": v(342.9, 41.28) * mm, "radius": 6.87 * mm, "construction": true});
            skLineSegment(sketch, "E24.24.0.5", {"start": v(339.46, 35.32) * mm, "end": v(336.03, 41.27) * mm});
            skLineSegment(sketch, "E24.24.0.6", {"start": v(336.03, 41.27) * mm, "end": v(339.46, 47.23) * mm});
            skLineSegment(sketch, "E24.25.0.0", {"start": v(422.54, 35.32) * mm, "end": v(415.66, 35.32) * mm});
            skLineSegment(sketch, "E24.25.0.1", {"start": v(425.97, 41.28) * mm, "end": v(422.54, 35.32) * mm});
            skLineSegment(sketch, "E24.25.0.2", {"start": v(415.66, 47.23) * mm, "end": v(422.54, 47.23) * mm});
            skLineSegment(sketch, "E24.25.0.3", {"start": v(422.54, 47.23) * mm, "end": v(425.97, 41.28) * mm});
            skCircle(sketch, "E24.25.0.4", {"center": v(419.1, 41.28) * mm, "radius": 6.87 * mm, "construction": true});
            skLineSegment(sketch, "E24.25.0.5", {"start": v(415.66, 35.32) * mm, "end": v(412.23, 41.27) * mm});
            skLineSegment(sketch, "E24.25.0.6", {"start": v(412.23, 41.27) * mm, "end": v(415.66, 47.23) * mm});
            skLineSegment(sketch, "E24.26.0.0", {"start": v(498.74, 35.32) * mm, "end": v(491.86, 35.32) * mm});
            skLineSegment(sketch, "E24.26.0.1", {"start": v(502.17, 41.28) * mm, "end": v(498.74, 35.32) * mm});
            skLineSegment(sketch, "E24.26.0.2", {"start": v(491.86, 47.23) * mm, "end": v(498.74, 47.23) * mm});
            skLineSegment(sketch, "E24.26.0.3", {"start": v(498.74, 47.23) * mm, "end": v(502.17, 41.28) * mm});
            skCircle(sketch, "E24.26.0.4", {"center": v(495.3, 41.28) * mm, "radius": 6.87 * mm, "construction": true});
            skLineSegment(sketch, "E24.26.0.5", {"start": v(491.86, 35.32) * mm, "end": v(488.43, 41.27) * mm});
            skLineSegment(sketch, "E24.26.0.6", {"start": v(488.43, 41.27) * mm, "end": v(491.86, 47.23) * mm});
            skLineSegment(sketch, "E24.27.0.0", {"start": v(574.94, 35.32) * mm, "end": v(568.06, 35.32) * mm});
            skLineSegment(sketch, "E24.27.0.1", {"start": v(578.37, 41.28) * mm, "end": v(574.94, 35.32) * mm});
            skLineSegment(sketch, "E24.27.0.2", {"start": v(568.06, 47.23) * mm, "end": v(574.94, 47.23) * mm});
            skLineSegment(sketch, "E24.27.0.3", {"start": v(574.94, 47.23) * mm, "end": v(578.37, 41.28) * mm});
            skCircle(sketch, "E24.27.0.4", {"center": v(571.5, 41.28) * mm, "radius": 6.87 * mm, "construction": true});
            skLineSegment(sketch, "E24.27.0.5", {"start": v(568.06, 35.32) * mm, "end": v(564.63, 41.28) * mm});
            skLineSegment(sketch, "E24.27.0.6", {"start": v(564.63, 41.27) * mm, "end": v(568.06, 47.23) * mm});
            skLineSegment(sketch, "E24.28.0.0", {"start": v(651.14, 35.32) * mm, "end": v(644.26, 35.32) * mm});
            skLineSegment(sketch, "E24.28.0.1", {"start": v(654.57, 41.28) * mm, "end": v(651.14, 35.32) * mm});
            skLineSegment(sketch, "E24.28.0.2", {"start": v(644.26, 47.23) * mm, "end": v(651.14, 47.23) * mm});
            skLineSegment(sketch, "E24.28.0.3", {"start": v(651.14, 47.23) * mm, "end": v(654.57, 41.28) * mm});
            skCircle(sketch, "E24.28.0.4", {"center": v(647.7, 41.28) * mm, "radius": 6.87 * mm, "construction": true});
            skLineSegment(sketch, "E24.28.0.5", {"start": v(644.26, 35.32) * mm, "end": v(640.83, 41.28) * mm});
            skLineSegment(sketch, "E24.28.0.6", {"start": v(640.83, 41.27) * mm, "end": v(644.26, 47.23) * mm});
            skLineSegment(sketch, "E24.29.0.0", {"start": v(727.34, 35.32) * mm, "end": v(720.46, 35.32) * mm});
            skLineSegment(sketch, "E24.29.0.1", {"start": v(730.77, 41.28) * mm, "end": v(727.34, 35.32) * mm});
            skLineSegment(sketch, "E24.29.0.2", {"start": v(720.46, 47.23) * mm, "end": v(727.34, 47.23) * mm});
            skLineSegment(sketch, "E24.29.0.3", {"start": v(727.34, 47.23) * mm, "end": v(730.77, 41.28) * mm});
            skCircle(sketch, "E24.29.0.4", {"center": v(723.9, 41.28) * mm, "radius": 6.87 * mm, "construction": true});
            skLineSegment(sketch, "E24.29.0.5", {"start": v(720.46, 35.32) * mm, "end": v(717.03, 41.28) * mm});
            skLineSegment(sketch, "E24.29.0.6", {"start": v(717.03, 41.27) * mm, "end": v(720.46, 47.23) * mm});
            skLineSegment(sketch, "E24.30.0.0", {"start": v(803.54, 35.32) * mm, "end": v(796.66, 35.32) * mm});
            skLineSegment(sketch, "E24.30.0.1", {"start": v(806.97, 41.28) * mm, "end": v(803.54, 35.32) * mm});
            skLineSegment(sketch, "E24.30.0.2", {"start": v(796.66, 47.23) * mm, "end": v(803.54, 47.23) * mm});
            skLineSegment(sketch, "E24.30.0.3", {"start": v(803.54, 47.23) * mm, "end": v(806.97, 41.28) * mm});
            skCircle(sketch, "E24.30.0.4", {"center": v(800.1, 41.28) * mm, "radius": 6.87 * mm, "construction": true});
            skLineSegment(sketch, "E24.30.0.5", {"start": v(796.66, 35.32) * mm, "end": v(793.23, 41.28) * mm});
            skLineSegment(sketch, "E24.30.0.6", {"start": v(793.23, 41.27) * mm, "end": v(796.66, 47.23) * mm});
            skLineSegment(sketch, "E24.31.0.0", {"start": v(879.74, 35.32) * mm, "end": v(872.86, 35.32) * mm});
            skLineSegment(sketch, "E24.31.0.1", {"start": v(883.17, 41.28) * mm, "end": v(879.74, 35.32) * mm});
            skLineSegment(sketch, "E24.31.0.2", {"start": v(872.86, 47.23) * mm, "end": v(879.74, 47.23) * mm});
            skLineSegment(sketch, "E24.31.0.3", {"start": v(879.74, 47.23) * mm, "end": v(883.17, 41.28) * mm});
            skCircle(sketch, "E24.31.0.4", {"center": v(876.3, 41.28) * mm, "radius": 6.87 * mm, "construction": true});
            skLineSegment(sketch, "E24.31.0.5", {"start": v(872.86, 35.32) * mm, "end": v(869.43, 41.28) * mm});
            skLineSegment(sketch, "E24.31.0.6", {"start": v(869.43, 41.27) * mm, "end": v(872.86, 47.23) * mm});
            skLineSegment(sketch, "E24.32.0.0", {"start": v(955.94, 35.32) * mm, "end": v(949.06, 35.32) * mm});
            skLineSegment(sketch, "E24.32.0.1", {"start": v(959.37, 41.28) * mm, "end": v(955.94, 35.32) * mm});
            skLineSegment(sketch, "E24.32.0.2", {"start": v(949.06, 47.23) * mm, "end": v(955.94, 47.23) * mm});
            skLineSegment(sketch, "E24.32.0.3", {"start": v(955.94, 47.23) * mm, "end": v(959.37, 41.28) * mm});
            skCircle(sketch, "E24.32.0.4", {"center": v(952.5, 41.28) * mm, "radius": 6.87 * mm, "construction": true});
            skLineSegment(sketch, "E24.32.0.5", {"start": v(949.06, 35.32) * mm, "end": v(945.63, 41.28) * mm});
            skLineSegment(sketch, "E24.32.0.6", {"start": v(945.63, 41.27) * mm, "end": v(949.06, 47.23) * mm});
            skLineSegment(sketch, "E24.33.0.0", {"start": v(1032.14, 35.32) * mm, "end": v(1025.26, 35.32) * mm});
            skLineSegment(sketch, "E24.33.0.1", {"start": v(1035.57, 41.28) * mm, "end": v(1032.14, 35.32) * mm});
            skLineSegment(sketch, "E24.33.0.2", {"start": v(1025.26, 47.23) * mm, "end": v(1032.14, 47.23) * mm});
            skLineSegment(sketch, "E24.33.0.3", {"start": v(1032.14, 47.23) * mm, "end": v(1035.57, 41.28) * mm});
            skCircle(sketch, "E24.33.0.4", {"center": v(1028.7, 41.28) * mm, "radius": 6.87 * mm, "construction": true});
            skLineSegment(sketch, "E24.33.0.5", {"start": v(1025.26, 35.32) * mm, "end": v(1021.83, 41.28) * mm});
            skLineSegment(sketch, "E24.33.0.6", {"start": v(1021.83, 41.27) * mm, "end": v(1025.26, 47.23) * mm});
            skLineSegment(sketch, "E24.34.0.0", {"start": v(1108.34, 35.32) * mm, "end": v(1101.46, 35.32) * mm});
            skLineSegment(sketch, "E24.34.0.1", {"start": v(1111.77, 41.28) * mm, "end": v(1108.34, 35.32) * mm});
            skLineSegment(sketch, "E24.34.0.2", {"start": v(1101.46, 47.23) * mm, "end": v(1108.34, 47.23) * mm});
            skLineSegment(sketch, "E24.34.0.3", {"start": v(1108.34, 47.23) * mm, "end": v(1111.77, 41.28) * mm});
            skCircle(sketch, "E24.34.0.4", {"center": v(1104.9, 41.28) * mm, "radius": 6.87 * mm, "construction": true});
            skLineSegment(sketch, "E24.34.0.5", {"start": v(1101.46, 35.32) * mm, "end": v(1098.03, 41.27) * mm});
            skLineSegment(sketch, "E24.34.0.6", {"start": v(1098.03, 41.27) * mm, "end": v(1101.46, 47.23) * mm});
            skLineSegment(sketch, "E24.35.0.0", {"start": v(1184.54, 35.32) * mm, "end": v(1177.66, 35.32) * mm});
            skLineSegment(sketch, "E24.35.0.1", {"start": v(1187.97, 41.28) * mm, "end": v(1184.54, 35.32) * mm});
            skLineSegment(sketch, "E24.35.0.2", {"start": v(1177.66, 47.23) * mm, "end": v(1184.54, 47.23) * mm});
            skLineSegment(sketch, "E24.35.0.3", {"start": v(1184.54, 47.23) * mm, "end": v(1187.97, 41.28) * mm});
            skCircle(sketch, "E24.35.0.4", {"center": v(1181.1, 41.28) * mm, "radius": 6.87 * mm, "construction": true});
            skLineSegment(sketch, "E24.35.0.5", {"start": v(1177.66, 35.32) * mm, "end": v(1174.23, 41.28) * mm});
            skLineSegment(sketch, "E24.35.0.6", {"start": v(1174.23, 41.27) * mm, "end": v(1177.66, 47.23) * mm});
            skLineSegment(sketch, "E24.36.0.0", {"start": v(1260.74, 35.32) * mm, "end": v(1253.86, 35.32) * mm});
            skLineSegment(sketch, "E24.36.0.1", {"start": v(1264.17, 41.28) * mm, "end": v(1260.74, 35.32) * mm});
            skLineSegment(sketch, "E24.36.0.2", {"start": v(1253.86, 47.23) * mm, "end": v(1260.74, 47.23) * mm});
            skLineSegment(sketch, "E24.36.0.3", {"start": v(1260.74, 47.23) * mm, "end": v(1264.17, 41.28) * mm});
            skCircle(sketch, "E24.36.0.4", {"center": v(1257.3, 41.28) * mm, "radius": 6.87 * mm, "construction": true});
            skLineSegment(sketch, "E24.36.0.5", {"start": v(1253.86, 35.32) * mm, "end": v(1250.43, 41.28) * mm});
            skLineSegment(sketch, "E24.36.0.6", {"start": v(1250.43, 41.27) * mm, "end": v(1253.86, 47.23) * mm});
            skLineSegment(sketch, "E24.37.0.0", {"start": v(1336.94, 35.32) * mm, "end": v(1330.06, 35.32) * mm});
            skLineSegment(sketch, "E24.37.0.1", {"start": v(1340.37, 41.28) * mm, "end": v(1336.94, 35.32) * mm});
            skLineSegment(sketch, "E24.37.0.2", {"start": v(1330.06, 47.23) * mm, "end": v(1336.94, 47.23) * mm});
            skLineSegment(sketch, "E24.37.0.3", {"start": v(1336.94, 47.23) * mm, "end": v(1340.37, 41.28) * mm});
            skCircle(sketch, "E24.37.0.4", {"center": v(1333.5, 41.28) * mm, "radius": 6.87 * mm, "construction": true});
            skLineSegment(sketch, "E24.37.0.5", {"start": v(1330.06, 35.32) * mm, "end": v(1326.63, 41.28) * mm});
            skLineSegment(sketch, "E24.37.0.6", {"start": v(1326.63, 41.27) * mm, "end": v(1330.06, 47.23) * mm});
            skLineSegment(sketch, "E24.38.0.0", {"start": v(1413.14, 35.32) * mm, "end": v(1406.26, 35.32) * mm});
            skLineSegment(sketch, "E24.38.0.1", {"start": v(1416.57, 41.28) * mm, "end": v(1413.14, 35.32) * mm});
            skLineSegment(sketch, "E24.38.0.2", {"start": v(1406.26, 47.23) * mm, "end": v(1413.14, 47.23) * mm});
            skLineSegment(sketch, "E24.38.0.3", {"start": v(1413.14, 47.23) * mm, "end": v(1416.57, 41.28) * mm});
            skCircle(sketch, "E24.38.0.4", {"center": v(1409.7, 41.28) * mm, "radius": 6.87 * mm, "construction": true});
            skLineSegment(sketch, "E24.38.0.5", {"start": v(1406.26, 35.32) * mm, "end": v(1402.83, 41.27) * mm});
            skLineSegment(sketch, "E24.38.0.6", {"start": v(1402.83, 41.27) * mm, "end": v(1406.26, 47.23) * mm});
            skLineSegment(sketch, "E24.39.0.0", {"start": v(1489.34, 35.32) * mm, "end": v(1482.46, 35.32) * mm});
            skLineSegment(sketch, "E24.39.0.1", {"start": v(1492.77, 41.28) * mm, "end": v(1489.34, 35.32) * mm});
            skLineSegment(sketch, "E24.39.0.2", {"start": v(1482.46, 47.23) * mm, "end": v(1489.34, 47.23) * mm});
            skLineSegment(sketch, "E24.39.0.3", {"start": v(1489.34, 47.23) * mm, "end": v(1492.77, 41.28) * mm});
            skCircle(sketch, "E24.39.0.4", {"center": v(1485.9, 41.28) * mm, "radius": 6.87 * mm, "construction": true});
            skLineSegment(sketch, "E24.39.0.5", {"start": v(1482.46, 35.32) * mm, "end": v(1479.03, 41.28) * mm});
            skLineSegment(sketch, "E24.39.0.6", {"start": v(1479.03, 41.27) * mm, "end": v(1482.46, 47.23) * mm});
            skLineSegment(sketch, "E24.direction1", {"start": v(-1489.34, 35.32) * mm, "end": v(-1413.14, 35.32) * mm, "construction": true});
            skSolve(sketch);
        }
        {
            var Q0;
            Q0 = qSketchRegion(id + "F4", true);
            extrude(context, id + "F5", {"entities" : qUnion([Q0]), "operationType" : NewBodyOperationType.REMOVE, "oppositeDirection" : true, "depth" : 3.17 * mm});
        }
    });
